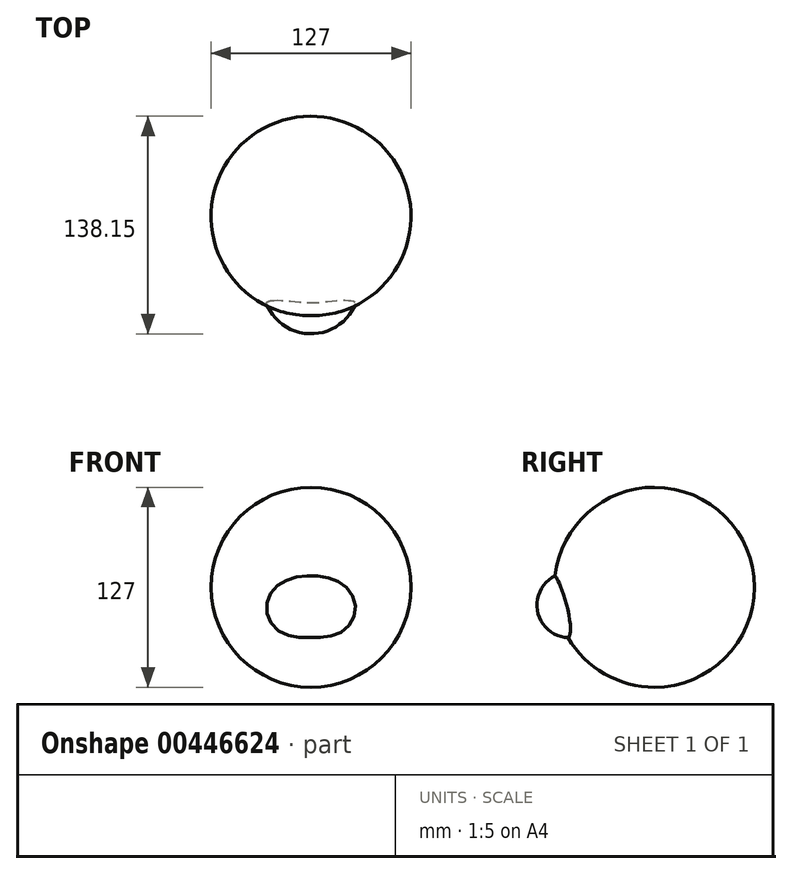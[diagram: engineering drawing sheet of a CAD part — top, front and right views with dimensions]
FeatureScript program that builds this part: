
annotation { "Feature Type Name" : "Feature", "Feature Type Description" : "" }
export const myFeature = defineFeature(function(context is Context, id is Id, definition is map)
    precondition{}
    {
        {
            var Q0;
            Q0=qCreatedBy(makeId("Front.planeOp"),FACE);
            var sketch = newSketch(context, id + "F0", { "sketchPlane" : qUnion([Q0])});
            skArc(sketch, "E0", {"start": v(0, -63.5) * mm, "mid": v(63.5, 0) * mm, "end": v(0, 63.5) * mm});
            skLineSegment(sketch, "E1", {"start": v(0, 0) * mm, "end": v(0, 96.45) * mm, "construction": true});
            skLineSegment(sketch, "E2", {"start": v(0, 63.5) * mm, "end": v(0, -63.5) * mm});
            skSolve(sketch);
        }
        {
            var Q0;
            Q0 = qSketchRegion(id + "F0", true);
            var Q1;
            Q1=sQuery(id+"F0.wireOp",EDGE,"E1");
            revolve(context, id + "F1", {"entities" : qUnion([Q0]), "axis" : qUnion([Q1]), "revolveType" : RevolveType.FULL});
        }
        {
            var Q0;
            Q0=qCreatedBy(makeId("Right.planeOp"),FACE);
            var sketch = newSketch(context, id + "F2", { "sketchPlane" : qUnion([Q0])});
            skLineSegment(sketch, "E3", {"start": v(-44.13, 6.95) * mm, "end": v(-44.13, -29.54) * mm});
            skArc(sketch, "E4", {"start": v(-44.13, 6.95) * mm, "mid": v(-74.65, -11.3) * mm, "end": v(-44.13, -29.54) * mm});
            skSolve(sketch);
        }
        {
            var Q0;
            Q0 = qSketchRegion(id + "F2", true);
            var Q1;
            Q1=sQuery(id+"F2.wireOp",EDGE,"E3");
            revolve(context, id + "F3", {"operationType" : NewBodyOperationType.ADD, "entities" : qUnion([Q0]), "axis" : qUnion([Q1]), "revolveType" : RevolveType.FULL});
        }
    });
